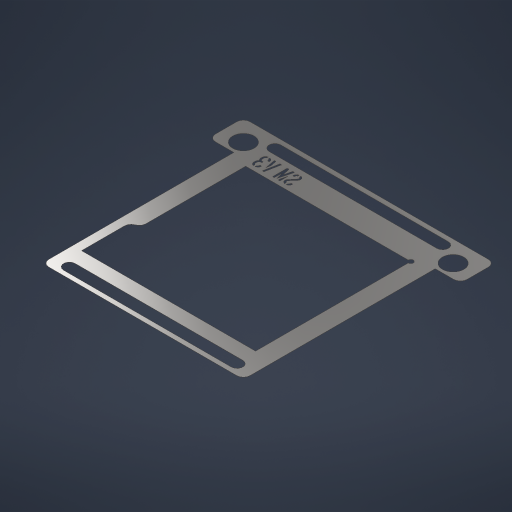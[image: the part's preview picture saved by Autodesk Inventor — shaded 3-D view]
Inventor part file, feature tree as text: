
AUTODESK INVENTOR PART (.ipt)
format: ipt  version: 2024 (Build 280153000, 153)  size: 473,088 bytes
history: native  units: in
note: dims shown in document units (in); Inventor stores cm internally (conversion verified against a paired STEP export)
features: extrude x5, sketch x2, hole x1, fillet x1, emboss x1
ambient origin geometry x8: Origin, YZ Plane, XZ Plane, XY Plane, X Axis, Y Axis, Z Axis, Center Point
bodies: Solid1 (feature_tree)
feature tree (10):
  extrude  "Extrusion1"  Depth=2.7in
  extrude  "Extrusion2"  TaperAngle=0.0deg  [1 undecoded]
  extrude  "Extrusion3"  Depth=0.3in
  hole  "Hole1"  [1 undecoded]
  extrude  "Extrusion4"  Depth=0.1378in
  extrude  "Extrusion5"  Depth=0.1378in
  fillet  "Fillet1"  Radius=2.0in
  emboss  "Emboss2"
  sketch  "Sketch2"  dims[d0=3.0in d1=2.7in]
  sketch  "Sketch8"  dims[d2=0.002in d3=0.0in d7=0.0in d8=0.0in d14=0.3in d16=0.4134in d17=0.1378in d18=0.1378in d19=2.0in d20=2.0in d21=0.125in d22=0.125in d23=1.0in d24=0.0in d27=0.0in d28=0.0in d29=0.0625in d30=0.5906in d31=0.2116in d32=0.1058in d33=0.0in d34=0.0in d39=1.8504in d40=1.9685in d41=0.25in d42=0.25in d43=0.25in d44=0.255in d45=0.2362in d46=0.1575in d47=0.0787in d48=90.0deg d49=0.315in d50=0.8108in d51=0.0787in d52=0.075in d53=0.225in d54=0.0098in d55=0.1949in d58=0.0394in d59=0.0in]
note: 2 required parameter values undecoded (feature->parameter linkage not recoverable at this tier; creation-order binding heuristic only, values carry confidence <= 0.55)
